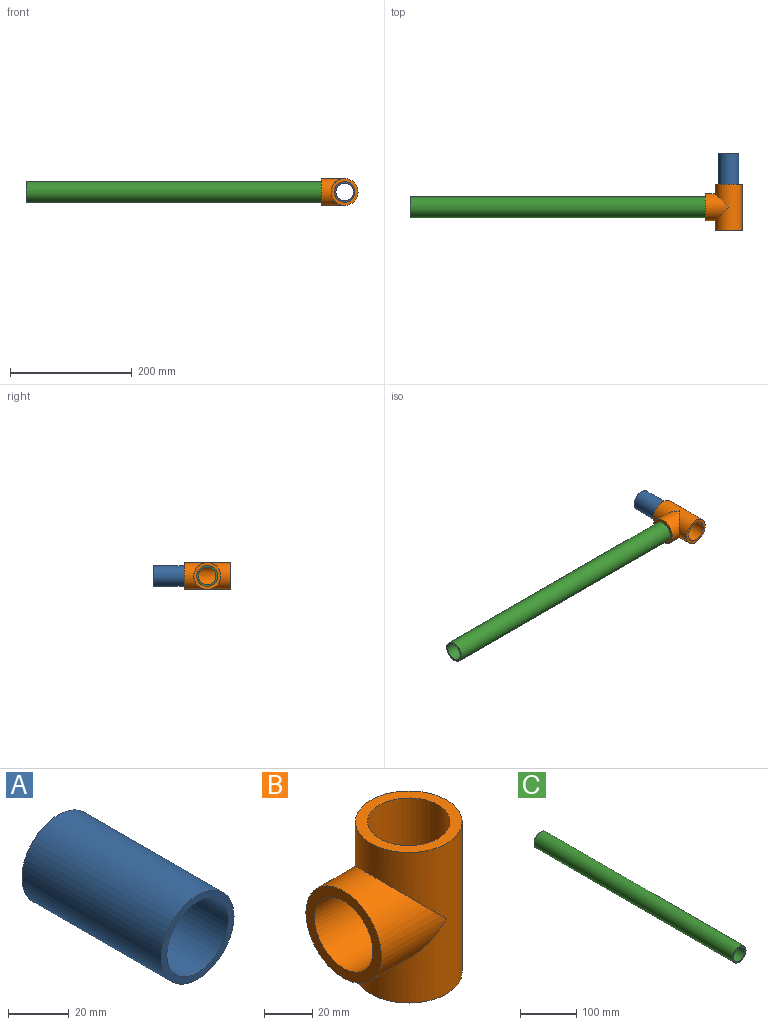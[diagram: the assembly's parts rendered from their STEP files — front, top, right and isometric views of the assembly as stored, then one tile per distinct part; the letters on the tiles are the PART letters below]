
ASSEMBLY  parts=3 mates=2
PART A: 4 faces, bbox 34x65x34 mm
  f0: cylinder r=14.35mm len=65mm, axis (0,1,0), area 5860.6mm2, adj f2,f3
  f1: cylinder r=17mm len=65mm, axis (0,1,0), area 6942.9mm2, adj f2,f3
  f2: plane 34x34mm, normal (0,-1,0), area 261mm2, adj f0,f1
  f3: plane 34x34mm, normal (0,1,0), area 261mm2, adj f0,f1
PART B: 7 faces, bbox 60x44x76 mm
  f0: cylinder r=17mm len=76mm, axis (0,0,1), area 6961.9mm2, adj f1,f2,f6
  f1: plane 44x44mm, normal (0,0,-1), area 612.6mm2, adj f0,f3
  f2: plane 44x44mm, normal (0,0,1), area 612.6mm2, adj f0,f3
  f3: cylinder r=22mm len=76mm, axis (0,0,1), area 8569.5mm2, adj f1,f2,f4
  f4: cylinder r=22mm len=44mm, axis (1,0,0), area 3316.7mm2, adj f3,f5
  f5: plane 44x44mm, normal (-1,0,0), area 612.6mm2, adj f4,f6
  f6: cylinder r=17mm len=38mm, axis (-1,0,0), area 2902.9mm2, adj f0,f5
PART C: 4 faces, bbox 34x500x34 mm
  f0: cylinder r=14.35mm len=500mm, axis (0,1,0), area 45081.9mm2, adj f2,f3
  f1: cylinder r=17mm len=500mm, axis (0,1,0), area 53407.1mm2, adj f2,f3
  f2: plane 34x34mm, normal (0,-1,0), area 261mm2, adj f0,f1
  f3: plane 34x34mm, normal (0,1,0), area 261mm2, adj f0,f1
PLACE A rot(axis=(1,0,0),180deg) t=(84.27,1957,-2568.64)mm
PLACE B rot(axis=(-1,0,0),90deg) t=(84.27,1934,-2568.64)mm
PLACE C rot(axis=(0.71,0.71,0),180deg) t=(61.27,1934,-2568.64)mm
MATE fastened C.f0 <-> B.f4  axis (1,0,0) through (61.27,1934,-2568.64)mm
MATE fastened A.f0 <-> B.f0  axis (0,-1,0) through (84.27,1957,-2568.64)mm
